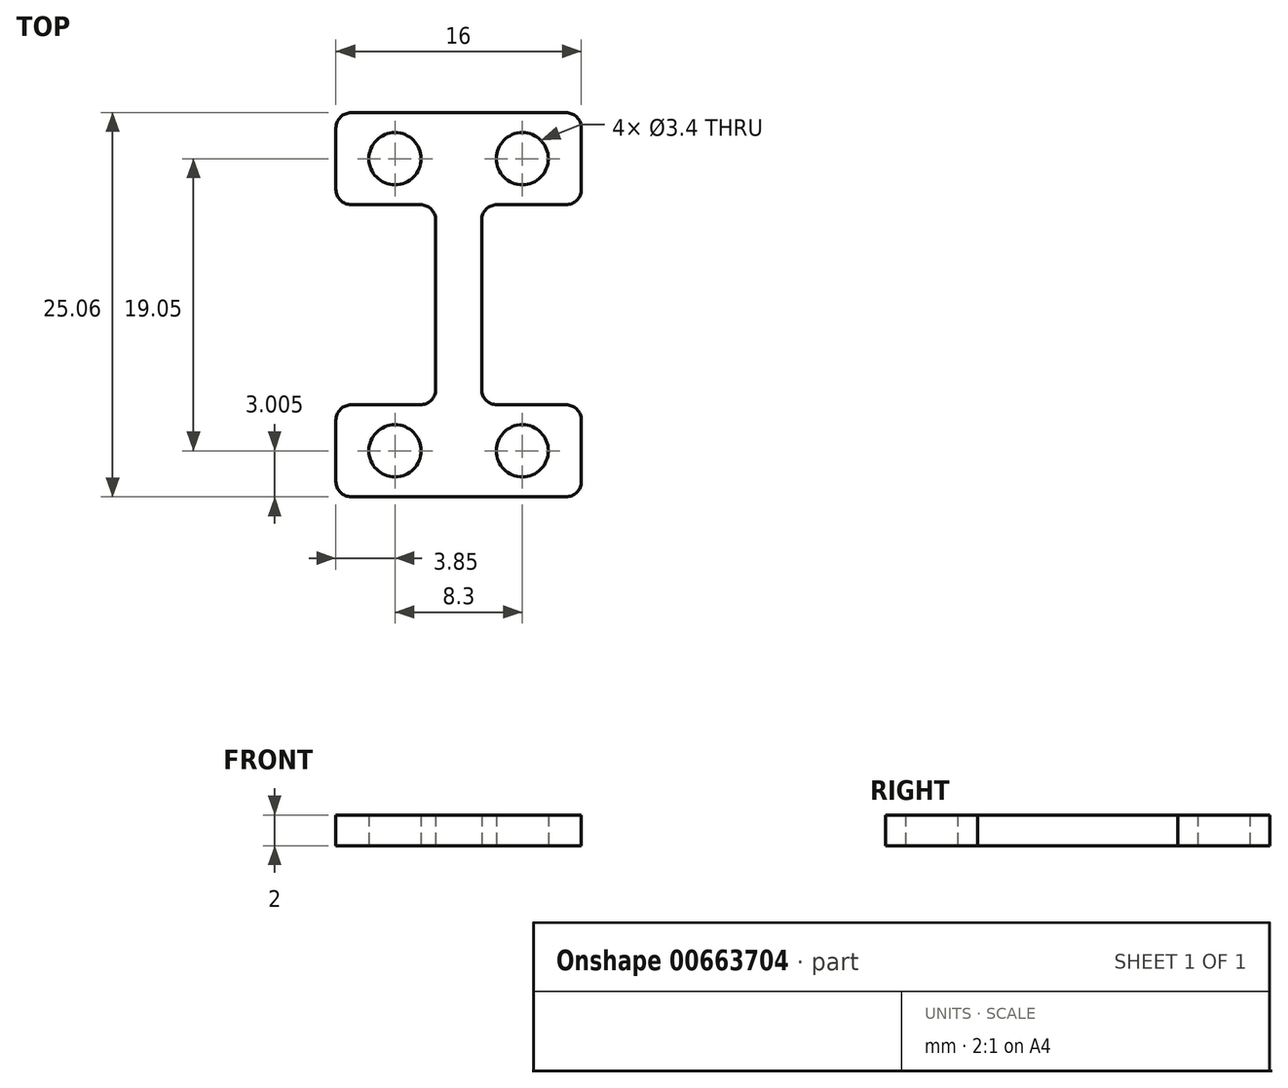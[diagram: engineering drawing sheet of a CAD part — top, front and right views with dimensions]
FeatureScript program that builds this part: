
annotation { "Feature Type Name" : "Feature", "Feature Type Description" : "" }
export const myFeature = defineFeature(function(context is Context, id is Id, definition is map)
    precondition{}
    {
        {
            var Q0;
            Q0=qCreatedBy(makeId("Top.planeOp"),FACE);
            var sketch = newSketch(context, id + "F0", { "sketchPlane" : qUnion([Q0])});
            skPoint(sketch, "E0.middle", {"position": v(0, 0) * mm});
            skCircle(sketch, "E1", {"center": v(4.15, 9.53) * mm, "radius": 1.7 * mm});
            skCircle(sketch, "E2.MirrorC", {"center": v(4.15, -9.53) * mm, "radius": 1.7 * mm});
            skCircle(sketch, "E3.MirrorC", {"center": v(-4.15, 9.53) * mm, "radius": 1.7 * mm});
            skCircle(sketch, "E4.MirrorC", {"center": v(-4.15, -9.53) * mm, "radius": 1.7 * mm});
            skLineSegment(sketch, "E5", {"start": v(-4.15, -9.53) * mm, "end": v(4.15, -9.52) * mm, "construction": true});
            skLineSegment(sketch, "E6", {"start": v(1.5, 5.52) * mm, "end": v(1.5, -5.52) * mm});
            skLineSegment(sketch, "E7.0", {"start": v(-1.5, 9.52) * mm, "end": v(-1.5, -9.53) * mm});
            skLineSegment(sketch, "E8", {"start": v(-7, -12.53) * mm, "end": v(7, -12.53) * mm});
            skLineSegment(sketch, "E9.MirrorCS", {"start": v(2.5, -6.52) * mm, "end": v(7, -6.52) * mm});
            skLineSegment(sketch, "E10", {"start": v(8, -11.53) * mm, "end": v(8, -7.52) * mm});
            skPoint(sketch, "E11.newPointA", {"position": v(9.7, -6.52) * mm});
            skArc(sketch, "E11.filletArc", {"start": v(8, -7.52) * mm, "mid": v(7.7, -6.82) * mm, "end": v(7, -6.52) * mm});
            skPoint(sketch, "E12.newPointA", {"position": v(9.7, -12.53) * mm});
            skArc(sketch, "E12.filletArc", {"start": v(7, -12.53) * mm, "mid": v(7.7, -12.23) * mm, "end": v(8, -11.53) * mm});
            skPoint(sketch, "E13.newPointA", {"position": v(-8, -6.52) * mm});
            skArc(sketch, "E13.filletArc", {"start": v(1.5, -5.52) * mm, "mid": v(1.8, -6.23) * mm, "end": v(2.5, -6.52) * mm});
            skArc(sketch, "E14.MirrorCS", {"start": v(1.5, 5.52) * mm, "mid": v(1.8, 6.23) * mm, "end": v(2.5, 6.52) * mm});
            skLineSegment(sketch, "E15.MirrorCS", {"start": v(2.5, 6.52) * mm, "end": v(7, 6.52) * mm});
            skArc(sketch, "E16.MirrorCS", {"start": v(8, 7.52) * mm, "mid": v(7.7, 6.82) * mm, "end": v(7, 6.52) * mm});
            skLineSegment(sketch, "E17.MirrorCS", {"start": v(8, 11.53) * mm, "end": v(8, 7.52) * mm});
            skArc(sketch, "E18.MirrorCS", {"start": v(7, 12.53) * mm, "mid": v(7.7, 12.23) * mm, "end": v(8, 11.53) * mm});
            skLineSegment(sketch, "E19.MirrorCS", {"start": v(-7, 12.53) * mm, "end": v(7, 12.53) * mm});
            skArc(sketch, "E20.MirrorCS", {"start": v(-1.5, 5.52) * mm, "mid": v(-1.8, 6.23) * mm, "end": v(-2.5, 6.52) * mm});
            skLineSegment(sketch, "E21.MirrorCS", {"start": v(-2.5, 6.52) * mm, "end": v(-7, 6.52) * mm});
            skLineSegment(sketch, "E22.MirrorCS", {"start": v(-8, 11.53) * mm, "end": v(-8, 7.52) * mm});
            skArc(sketch, "E23.MirrorCS", {"start": v(-7, 12.53) * mm, "mid": v(-7.7, 12.23) * mm, "end": v(-8, 11.53) * mm});
            skArc(sketch, "E24.MirrorCS", {"start": v(-8, 7.52) * mm, "mid": v(-7.7, 6.82) * mm, "end": v(-7, 6.52) * mm});
            skLineSegment(sketch, "E25.MirrorCS", {"start": v(-2.5, -6.52) * mm, "end": v(-7, -6.52) * mm});
            skArc(sketch, "E26.MirrorCS", {"start": v(-1.5, -5.52) * mm, "mid": v(-1.8, -6.23) * mm, "end": v(-2.5, -6.52) * mm});
            skArc(sketch, "E27.MirrorCS", {"start": v(-8, -7.52) * mm, "mid": v(-7.7, -6.82) * mm, "end": v(-7, -6.52) * mm});
            skLineSegment(sketch, "E28.MirrorCS", {"start": v(-8, -11.53) * mm, "end": v(-8, -7.52) * mm});
            skArc(sketch, "E29.MirrorCS", {"start": v(-7, -12.53) * mm, "mid": v(-7.7, -12.23) * mm, "end": v(-8, -11.53) * mm});
            skPoint(sketch, "E30.orphan", {"position": v(-8, -12.53) * mm});
            skPoint(sketch, "E31.orphan", {"position": v(-8, 12.53) * mm});
            skPoint(sketch, "E32.orphan", {"position": v(1.5, 9.52) * mm});
            skSolve(sketch);
        }
        {
            var Q0;
            Q0=makeQuery(id+"F0.imprint","IMPRINT",FACE,{"disambiguationData":[TD([[makeQuery(id+"F0.imprint","IMPRINT",EDGE,{"derivedFrom":sQuery(id+"F0.wireOp",EDGE,"E1")}),-1.0]])]});
            extrude(context, id + "F1", {"entities" : qUnion([Q0]), "depth" : 2 * mm, "offsetDistance" : 25 * mm});
        }
    });
